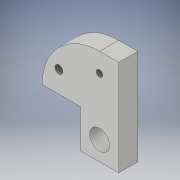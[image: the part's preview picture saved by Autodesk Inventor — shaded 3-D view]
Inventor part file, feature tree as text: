
AUTODESK INVENTOR PART (.ipt)
format: ipt  version: 2019 (Build 230136000, 136)  size: 131,072 bytes
history: native  units: in
note: dims shown in document units (in); Inventor stores cm internally (conversion verified against a paired STEP export)
features: sketch x4, hole x3, extrude x1, fillet x1
ambient origin geometry x8: Origin, YZ Plane, XZ Plane, XY Plane, X Axis, Y Axis, Z Axis, Center Point
bodies: Solid1 (feature_tree)
feature tree (9):
  extrude  "Extrusion1"  Depth=0.75in
  fillet  "Fillet1"  Radius=0.75in
  hole  "Hole1"  [1 undecoded]
  hole  "Hole2"  [1 undecoded]
  hole  "Hole3"  [1 undecoded]
  sketch  "Sketch1"  dims[d1=1.25in d2=1.0in d3=0.75in]
  sketch  "Sketch2"  dims[d4=0.5in d5=0.5in]
  sketch  "Sketch3"  dims[d8=0.25in d9=0.0in d10=0.75in]
  sketch  "Sketch4"  dims[d11=0.25in d12=0.25in d13=0.26in d14=0.276in d15=0.375in d16=0.25in d17=0.5635in d18=1.0in d19=0.8108in d20=0.25in d21=0.25in d22=0.085in d23=0.224in d24=0.375in d25=0.25in d26=0.5635in d27=0.349in d28=0.8108in d29=1.5in d30=45.0deg d31=0.104in d32=0.276in d33=0.375in d34=0.25in d35=0.5635in d36=0.432in d37=0.8108in]
note: 3 required parameter values undecoded (feature->parameter linkage not recoverable at this tier; creation-order binding heuristic only, values carry confidence <= 0.55)
